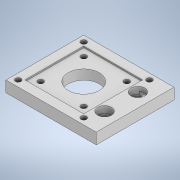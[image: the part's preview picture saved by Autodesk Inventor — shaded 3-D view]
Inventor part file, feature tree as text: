
AUTODESK INVENTOR PART (.ipt)
format: ipt  version: 2022 (Build 260153000, 153)  size: 214,016 bytes
history: native  units: mm
features: extrude x4, sketch x4, projected_geometry x1
ambient origin geometry x8: Origin, YZ Plane, XZ Plane, XY Plane, X Axis, Y Axis, Z Axis, Center Point
bodies: Solid1 (feature_tree)
feature tree (9):
  extrude  "Extrusion1"  Depth=65.0mm
  extrude  "Extrusion2"  Depth=22.3mm
  extrude  "Extrusion3"  Depth=31.0mm
  extrude  "Extrusion4"  Depth=4.0mm
  sketch  "Sketch1"  dims[d0=56.0mm d1=65.0mm]
  sketch  "Sketch2"  dims[d2=28.0mm d3=22.3mm]
  sketch  "Sketch3"  dims[d4=31.0mm d5=31.0mm]
  sketch  "Sketch4"  dims[d6=40.0mm d8=360.0deg d10=4.0mm d11=11.5mm d12=4.0mm d13=40.0mm d15=360.0deg d17=16.0mm d18=10.0mm d19=6.3mm d20=8.0mm d21=0.0mm d22=42.3mm d23=42.3mm d24=1.0mm d25=0.0mm d26=10.0mm d27=10.0mm d28=5.0mm d29=0.0mm d30=6.0mm d31=40.0mm d33=360.0deg d35=9.5mm d36=11.5mm d37=6.0mm d38=5.0mm d39=0.0mm]
  projected_geometry  "Projected Loop1"
